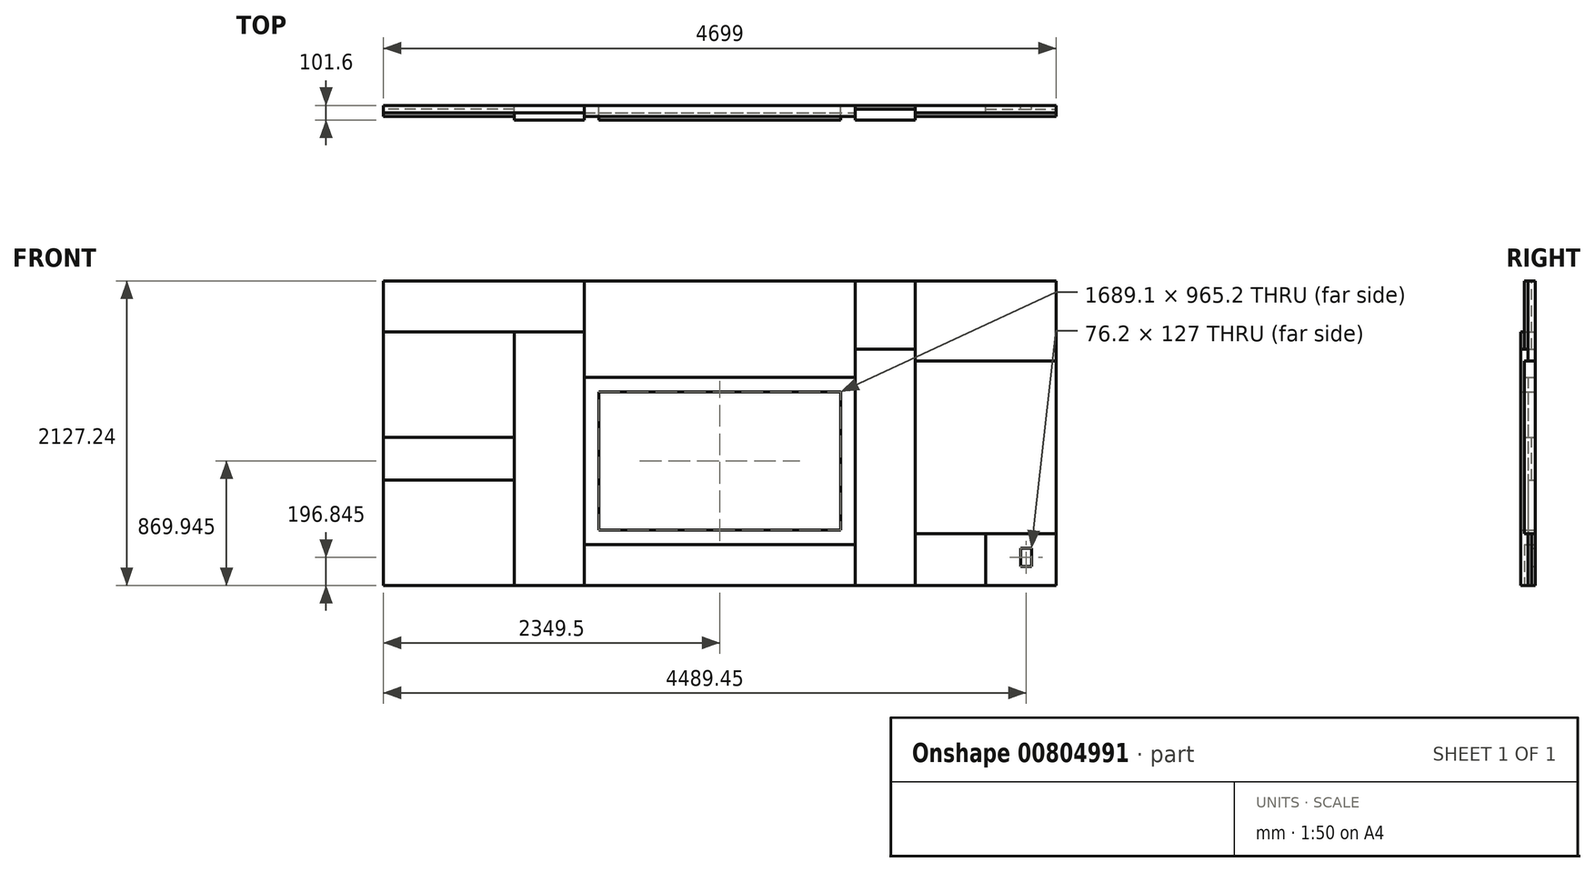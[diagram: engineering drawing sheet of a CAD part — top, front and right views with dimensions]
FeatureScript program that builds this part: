
annotation { "Feature Type Name" : "Feature", "Feature Type Description" : "" }
export const myFeature = defineFeature(function(context is Context, id is Id, definition is map)
    precondition{}
    {
        {
            var Q0;
            Q0=qCreatedBy(makeId("Front.planeOp"),FACE);
            var sketch = newSketch(context, id + "F0", { "sketchPlane" : qUnion([Q0])});
            skLineSegment(sketch, "E0.bottom", {"start": v(2349.5, -1063.62) * mm, "end": v(-2349.5, -1063.63) * mm});
            skLineSegment(sketch, "E0.top", {"start": v(2349.5, 1063.63) * mm, "end": v(-2349.5, 1063.63) * mm});
            skLineSegment(sketch, "E0.left", {"start": v(2349.5, -1063.62) * mm, "end": v(2349.5, 1063.63) * mm});
            skLineSegment(sketch, "E0.right", {"start": v(-2349.5, -1063.63) * mm, "end": v(-2349.5, 1063.63) * mm});
            skPoint(sketch, "E0.middle", {"position": v(0, 0) * mm});
            skLineSegment(sketch, "E1", {"start": v(-2349.5, 708.02) * mm, "end": v(-946.15, 708.02) * mm});
            skLineSegment(sketch, "E2", {"start": v(-946.15, 708.02) * mm, "end": v(-946.15, 1063.62) * mm});
            skLineSegment(sketch, "E3", {"start": v(-2349.5, -28.58) * mm, "end": v(-1435.1, -28.58) * mm});
            skLineSegment(sketch, "E4", {"start": v(-1435.1, -28.58) * mm, "end": v(-1435.1, 708.02) * mm});
            skLineSegment(sketch, "E5", {"start": v(-1435.1, -28.58) * mm, "end": v(-1435.1, -327.03) * mm});
            skLineSegment(sketch, "E6", {"start": v(-1435.1, -327.03) * mm, "end": v(-2349.5, -327.03) * mm});
            skLineSegment(sketch, "E7", {"start": v(-1435.1, -327.03) * mm, "end": v(-1435.1, -1063.63) * mm});
            skLineSegment(sketch, "E8", {"start": v(-1435.1, -1063.63) * mm, "end": v(-2349.5, -1063.63) * mm});
            skLineSegment(sketch, "E9", {"start": v(-946.15, 708.03) * mm, "end": v(-946.15, -1063.63) * mm});
            skLineSegment(sketch, "E10", {"start": v(-946.15, 390.52) * mm, "end": v(946.15, 390.52) * mm});
            skLineSegment(sketch, "E11", {"start": v(946.15, 390.52) * mm, "end": v(946.15, 1063.62) * mm});
            skLineSegment(sketch, "E12", {"start": v(946.15, 390.52) * mm, "end": v(946.15, -777.87) * mm});
            skLineSegment(sketch, "E13", {"start": v(946.15, -777.87) * mm, "end": v(-946.15, -777.87) * mm});
            skLineSegment(sketch, "E14", {"start": v(946.15, -777.87) * mm, "end": v(946.15, -1063.62) * mm});
            skLineSegment(sketch, "E15", {"start": v(1365.25, -1063.62) * mm, "end": v(1365.25, 587.38) * mm});
            skLineSegment(sketch, "E16", {"start": v(1365.25, 587.38) * mm, "end": v(946.15, 587.38) * mm});
            skLineSegment(sketch, "E17", {"start": v(1365.25, 587.38) * mm, "end": v(1365.25, 1063.63) * mm});
            skLineSegment(sketch, "E18", {"start": v(1365.25, 504.83) * mm, "end": v(2349.5, 504.83) * mm});
            skLineSegment(sketch, "E19", {"start": v(1365.25, -701.67) * mm, "end": v(2349.5, -701.67) * mm});
            skLineSegment(sketch, "E20", {"start": v(1857.38, -701.67) * mm, "end": v(1857.38, -1063.62) * mm});
            skLineSegment(sketch, "E21.bottom", {"start": v(-844.55, 288.93) * mm, "end": v(844.55, 288.93) * mm});
            skLineSegment(sketch, "E21.top", {"start": v(-844.55, -676.27) * mm, "end": v(844.55, -676.27) * mm});
            skLineSegment(sketch, "E21.left", {"start": v(-844.55, 288.93) * mm, "end": v(-844.55, -676.27) * mm});
            skLineSegment(sketch, "E21.right", {"start": v(844.55, 288.93) * mm, "end": v(844.55, -676.27) * mm});
            skPoint(sketch, "E22", {"position": v(0, 288.93) * mm});
            skPoint(sketch, "E23", {"position": v(0, 390.52) * mm});
            skPoint(sketch, "E24", {"position": v(946.15, -193.67) * mm});
            skPoint(sketch, "E25", {"position": v(844.55, -193.67) * mm});
            skLineSegment(sketch, "E26.bottom", {"start": v(2101.85, -803.28) * mm, "end": v(2178.05, -803.28) * mm});
            skLineSegment(sketch, "E26.top", {"start": v(2101.85, -930.28) * mm, "end": v(2178.05, -930.28) * mm});
            skLineSegment(sketch, "E26.left", {"start": v(2101.85, -803.28) * mm, "end": v(2101.85, -930.28) * mm});
            skLineSegment(sketch, "E26.right", {"start": v(2178.05, -803.28) * mm, "end": v(2178.05, -930.28) * mm});
            skSolve(sketch);
        }
        {
            var Q0;
            {var subQ0=sQuery(id+"F0.wireOp",EDGE,"E4");Q0=makeQuery(id+"F0.imprint","IMPRINT",FACE,{"disambiguationData":[TD([[makeQuery(id+"F0.imprint","IMPRINT",EDGE,{"derivedFrom":subQ0}),-1.0]])]});}
            extrude(context, id + "F1", {"entities" : qUnion([Q0]), "depth" : 101.6 * mm, "offsetDistance" : 25.4 * mm});
        }
        {
            var Q0;
            {var subQ3=sQuery(id+"F0.wireOp",EDGE,"E3");Q0=makeQuery(id+"F0.imprint","IMPRINT",FACE,{"disambiguationData":[TD([[makeQuery(id+"F0.imprint","IMPRINT",EDGE,{"derivedFrom":subQ3}),1.0]])]});}
            extrude(context, id + "F2", {"entities" : qUnion([Q0]), "depth" : 76.2 * mm, "offsetDistance" : 25.4 * mm});
        }
        {
            var Q0;
            {var subQ0=sQuery(id+"F0.wireOp",EDGE,"E10");Q0=makeQuery(id+"F0.imprint","IMPRINT",FACE,{"disambiguationData":[TD([[makeQuery(id+"F0.imprint","IMPRINT",EDGE,{"derivedFrom":subQ0}),-1.0]])]});}
            extrude(context, id + "F3", {"entities" : qUnion([Q0]), "depth" : 50.8 * mm, "offsetDistance" : 25.4 * mm});
        }
        {
            var Q0;
            {var subQ0=sQuery(id+"F0.wireOp",EDGE,"E3");Q0=makeQuery(id+"F0.imprint","IMPRINT",FACE,{"disambiguationData":[TD([[makeQuery(id+"F0.imprint","IMPRINT",EDGE,{"derivedFrom":subQ0}),-1.0]])]});}
            extrude(context, id + "F4", {"entities" : qUnion([Q0]), "depth" : 25.4 * mm, "offsetDistance" : 25.4 * mm});
        }
        {
            var Q0;
            {var subQ2=sQuery(id+"F0.wireOp",EDGE,"E6");Q0=makeQuery(id+"F0.imprint","IMPRINT",FACE,{"disambiguationData":[TD([[makeQuery(id+"F0.imprint","IMPRINT",EDGE,{"derivedFrom":subQ2}),1.0]])]});}
            extrude(context, id + "F5", {"entities" : qUnion([Q0]), "depth" : 50.8 * mm, "offsetDistance" : 25.4 * mm});
        }
        {
            var Q0;
            {var subQ0=sQuery(id+"F0.wireOp",EDGE,"E2");Q0=makeQuery(id+"F0.imprint","IMPRINT",FACE,{"disambiguationData":[TD([[makeQuery(id+"F0.imprint","IMPRINT",EDGE,{"derivedFrom":subQ0}),1.0]])]});}
            extrude(context, id + "F6", {"entities" : qUnion([Q0]), "depth" : 50.8 * mm, "offsetDistance" : 25.4 * mm});
        }
        {
            var Q0;
            Q0=makeQuery(id+"F0.imprint","IMPRINT",FACE,{"disambiguationData":[TD([[makeQuery(id+"F0.imprint","IMPRINT",EDGE,{"derivedFrom":sQuery(id+"F0.wireOp",EDGE,"E21.bottom")}),-1.0]])]});
            extrude(context, id + "F7", {"entities" : qUnion([Q0]), "depth" : 101.6 * mm, "offsetDistance" : 25.4 * mm});
        }
        {
            var Q0;
            {var subQ1=sQuery(id+"F0.wireOp",EDGE,"E2");Q0=makeQuery(id+"F0.imprint","IMPRINT",FACE,{"disambiguationData":[TD([[makeQuery(id+"F0.imprint","IMPRINT",EDGE,{"derivedFrom":subQ1}),-1.0]])]});}
            extrude(context, id + "F8", {"entities" : qUnion([Q0]), "depth" : 76.2 * mm, "offsetDistance" : 25.4 * mm});
        }
        {
            var Q0;
            {var subQ4=sQuery(id+"F0.wireOp",EDGE,"E13");Q0=makeQuery(id+"F0.imprint","IMPRINT",FACE,{"disambiguationData":[TD([[makeQuery(id+"F0.imprint","IMPRINT",EDGE,{"derivedFrom":subQ4}),1.0]])]});}
            extrude(context, id + "F9", {"entities" : qUnion([Q0]), "depth" : 76.2 * mm, "offsetDistance" : 25.4 * mm});
        }
        {
            var Q0;
            {var subQ4=sQuery(id+"F0.wireOp",EDGE,"E16");Q0=makeQuery(id+"F0.imprint","IMPRINT",FACE,{"disambiguationData":[TD([[makeQuery(id+"F0.imprint","IMPRINT",EDGE,{"derivedFrom":subQ4}),-1.0]])]});}
            extrude(context, id + "F10", {"entities" : qUnion([Q0]), "depth" : 25.4 * mm, "offsetDistance" : 25.4 * mm});
        }
        {
            var Q0;
            {var subQ1=sQuery(id+"F0.wireOp",EDGE,"E12");Q0=makeQuery(id+"F0.imprint","IMPRINT",FACE,{"disambiguationData":[TD([[makeQuery(id+"F0.imprint","IMPRINT",EDGE,{"derivedFrom":subQ1}),1.0]])]});}
            extrude(context, id + "F11", {"entities" : qUnion([Q0]), "depth" : 101.6 * mm, "offsetDistance" : 25.4 * mm});
        }
        {
            var Q0;
            {var subQ0=sQuery(id+"F0.wireOp",EDGE,"E17");Q0=makeQuery(id+"F0.imprint","IMPRINT",FACE,{"disambiguationData":[TD([[makeQuery(id+"F0.imprint","IMPRINT",EDGE,{"derivedFrom":subQ0}),-1.0]])]});}
            extrude(context, id + "F12", {"entities" : qUnion([Q0]), "depth" : 50.8 * mm, "offsetDistance" : 25.4 * mm});
        }
        {
            var Q0;
            {var subQ0=sQuery(id+"F0.wireOp",EDGE,"E18");Q0=makeQuery(id+"F0.imprint","IMPRINT",FACE,{"disambiguationData":[TD([[makeQuery(id+"F0.imprint","IMPRINT",EDGE,{"derivedFrom":subQ0}),-1.0]])]});}
            extrude(context, id + "F13", {"entities" : qUnion([Q0]), "depth" : 76.2 * mm, "offsetDistance" : 25.4 * mm});
        }
        {
            var Q0;
            {var subQ3=sQuery(id+"F0.wireOp",EDGE,"E20");Q0=makeQuery(id+"F0.imprint","IMPRINT",FACE,{"disambiguationData":[TD([[makeQuery(id+"F0.imprint","IMPRINT",EDGE,{"derivedFrom":subQ3}),-1.0]])]});}
            extrude(context, id + "F14", {"entities" : qUnion([Q0]), "depth" : 50.8 * mm, "offsetDistance" : 25.4 * mm});
        }
        {
            var Q0;
            {var subQ3=sQuery(id+"F0.wireOp",EDGE,"E20");Q0=makeQuery(id+"F0.imprint","IMPRINT",FACE,{"disambiguationData":[TD([[makeQuery(id+"F0.imprint","IMPRINT",EDGE,{"derivedFrom":subQ3}),1.0]])]});}
            extrude(context, id + "F15", {"entities" : qUnion([Q0]), "depth" : 25.4 * mm, "offsetDistance" : 25.4 * mm});
        }
    });
